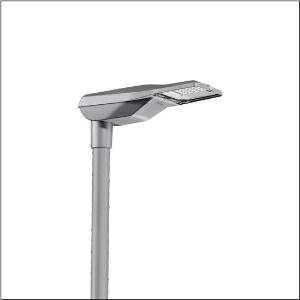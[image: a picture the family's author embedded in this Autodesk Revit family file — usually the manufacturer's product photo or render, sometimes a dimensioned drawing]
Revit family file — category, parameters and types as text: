
# Revit family: streetlight_sl_21_iq_micro___st1_0a_5xe1d31g08db_9cf9
name_source: partatom
category: Lighting Fixtures
units: mm (PartAtom-declared; Revit-internal decimal feet)

## family parameters
Cut with Voids When Loaded = No
Host = Face
Light Source = No
Part Type = Normal
Room Calculation Point = No
Round Connector Dimension = Use Diameter
Shared = No

## types (1)
- --- (1 x LED, 4810 lm, 36.4 W, 3000K)
    Apparent Load = 36 VA
    CIE Flux Codes = 37 72 97 100 100
    Color Rendering = 70
    Color Temperature = 3000K
    Default Elevation = 1800 mm
    Description = Streetlight SL 21 iQ micro, mast luminaire, primary light control with lens, of PMMA, primary optical cover: cover, of toughened safety glass, transparent, light distribution: ST1.0a, light emission: direct distribution, primary light characteristic: asymmetric, installation type: post-top, side-entry, LED, High Power LED, rated luminous flux: 4.810lm, luminous efficacy: 132lm/W, light colour: 730, colour temperature: 3000K, control: Street-Remote, Auto-Match, Temp-Guard, Lumen-Switch, Night-Set, Smart-Wire, Light-Fading, Desk-Remote (wireless, voltage-free reading and setting of iQ features in the workshop via application-optimized NFC function/RFID function), optimised constant luminous flux control (CLO 2.0), presetting dimming linear, mains connection: 220..240V, AC, 50/60Hz, start of lifetime: 36W, end of service life: 38W, reduction: 16W, luminaire housing, of diecast aluminium, powder-coated, Siteco® metallic grey (DB 702S), corrosivity category C5 mid according to DIN EN ISO 12944, please order mast flange separately, inclination adjustable: 0°, 5°, 10°, 15°, sealing non-destructively replaceable, multi-level sealing system, length: 528mm, width: 235mm, height: 110mm, mast flange for spigot size: 42mm (side-entry): 5XC10008XM4, 60/48mm (side-entry/post-top): 5XC10108XM2, 76/60mm (side-entry/post-top): 5XC10108XM1, protection rating (complete): IP66, insulation class (complete): insulation class II (safety insulation), certification: CE, ENEC, ENEC+, VDE, impact resistance: IK09, permissible operating ambient temperature for outdoor applications: -40..+50°C, standard-compliant lighting for roads and squares, packaging unit: 1 piece

Light Distribution: ST1.0a
    Height = 110 mm
    Lamp = 1 x LED
    Lamp Light Flux = 4810 lm
    Lamp Power = 36.4 W
    Lamp count = 1
    Length = 528 mm
    Luminous efficacy = 132 lm/W
    Manufacturer = Siteco
    ModVariant = No
    Model = 5XE1D31G08DB
    Number of Poles = 1
    OnlyDefault = Yes
    Power Factor = 1
    Product Name = Streetlight SL 21 iQ micro | ST1.0a
    Product group = mast luminaire | pylon top
    ProductGroupID = 6100
    Protection Class = Protection class II
    Protection Degree = IP 66
    RLX_Detail_Level = 1
    RLX_Emergency_Light_Flux = 0 lm
    RLX_Emergency_Type = 0
    RLX_Emergency_Type_DB = No
    RlxData = <blob elided: 98861 chars, md5=05c0a9e1>
    Socket = socket
    Standby Power = 0 W
    System Light Flux = 4810 lm
    System Power = 36 W
    Type Comments = factory setting: luminous flux: 100 % | dim-lin: 254 | 715 mA
    Type Image = l_1006881.jpg
    URL = http://relux.com
    VarID = @adj_088291
    Voltage = 0 V
    Weight = 0.00 kg
    Width = 235 mm

## geometry (parser evidence)
native form markers: Blend x4, Sweep x10
no freeform markers — native parametric forms only
